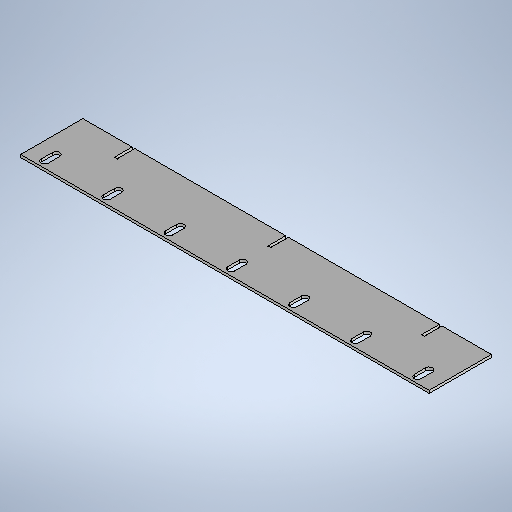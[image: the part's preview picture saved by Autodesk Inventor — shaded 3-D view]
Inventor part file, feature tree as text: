
AUTODESK INVENTOR PART (.ipt)
format: ipt  version: 2025.1 (Build 291241020, 241B)  size: 347,136 bytes
history: native  units: mm
features: other x4, sketch x3, pattern_linear x2, sheet_metal_op x1, projected_geometry x1
ambient origin geometry x8: Origin, YZ Plane, XZ Plane, XY Plane, X Axis, Y Axis, Z Axis, Center Point
bodies: Solid1 (feature_tree)
feature tree (11):
  sheet_metal_op  "Face1"
  pattern_linear  "Rectangular Pattern1"  Count1=46  [1 undecoded]
  pattern_linear  "Rectangular Pattern2"  Count1=7  [1 undecoded]
  sketch  "Sketch1"  dims[d2=3.0mm]
  other  "Plate1"
  sketch  "Sketch2"  dims[d3=8.0mm]
  projected_geometry  "Projected Loop1"
  sketch  "Sketch3"  dims[d5=7.0mm d6=3.0mm d7=0.0mm d8=70.0mm d10=70.0mm d11=3.1mm d12=20.0mm d13=3.0mm d14=0.0mm d15=30.0mm d17=173.0mm d22=13.0mm]
  other  "Cut1"
  other  "Cut2"
  other  "Definition1"
note: 2 required parameter values undecoded (feature->parameter linkage not recoverable at this tier; creation-order binding heuristic only, values carry confidence <= 0.55)
